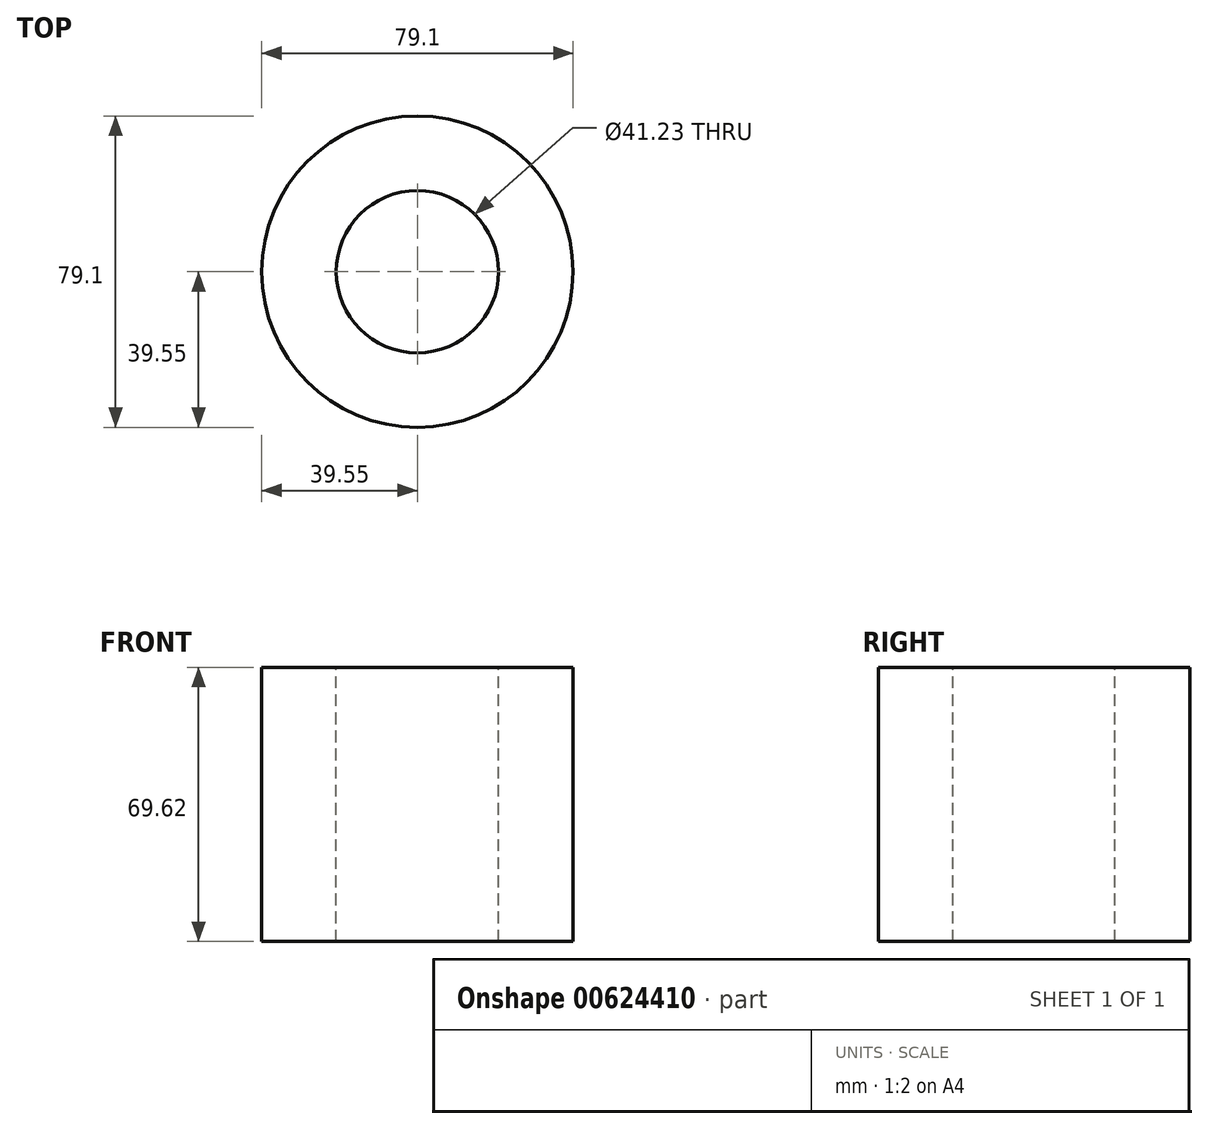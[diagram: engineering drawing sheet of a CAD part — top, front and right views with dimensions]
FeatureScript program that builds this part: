
annotation { "Feature Type Name" : "Feature", "Feature Type Description" : "" }
export const myFeature = defineFeature(function(context is Context, id is Id, definition is map)
    precondition{}
    {
        {
            var Q0;
            Q0=qCreatedBy(makeId("Right.planeOp"),FACE);
            var sketch = newSketch(context, id + "F0", { "sketchPlane" : qUnion([Q0])});
            skLineSegment(sketch, "E0.bottom", {"start": v(20.61, 37.71) * mm, "end": v(39.55, 37.71) * mm});
            skLineSegment(sketch, "E0.top", {"start": v(20.61, -31.91) * mm, "end": v(39.55, -31.91) * mm});
            skLineSegment(sketch, "E0.left", {"start": v(20.61, 37.71) * mm, "end": v(20.61, -31.91) * mm});
            skLineSegment(sketch, "E0.right", {"start": v(39.55, 37.71) * mm, "end": v(39.55, -31.91) * mm});
            skLineSegment(sketch, "E1", {"start": v(0, 58.48) * mm, "end": v(0, -59.4) * mm});
            skSolve(sketch);
        }
        {
            var Q0;
            Q0=makeQuery(id+"F0.imprint","IMPRINT",FACE,{"disambiguationData":[TD([[makeQuery(id+"F0.imprint","IMPRINT",EDGE,{"derivedFrom":sQuery(id+"F0.wireOp",EDGE,"E0.bottom")}),-1.0]])]});
            var Q1;
            Q1=sQuery(id+"F0.wireOp",EDGE,"E1");
            revolve(context, id + "F1", {"entities" : qUnion([Q0]), "axis" : qUnion([Q1]), "revolveType" : RevolveType.FULL});
        }
    });
